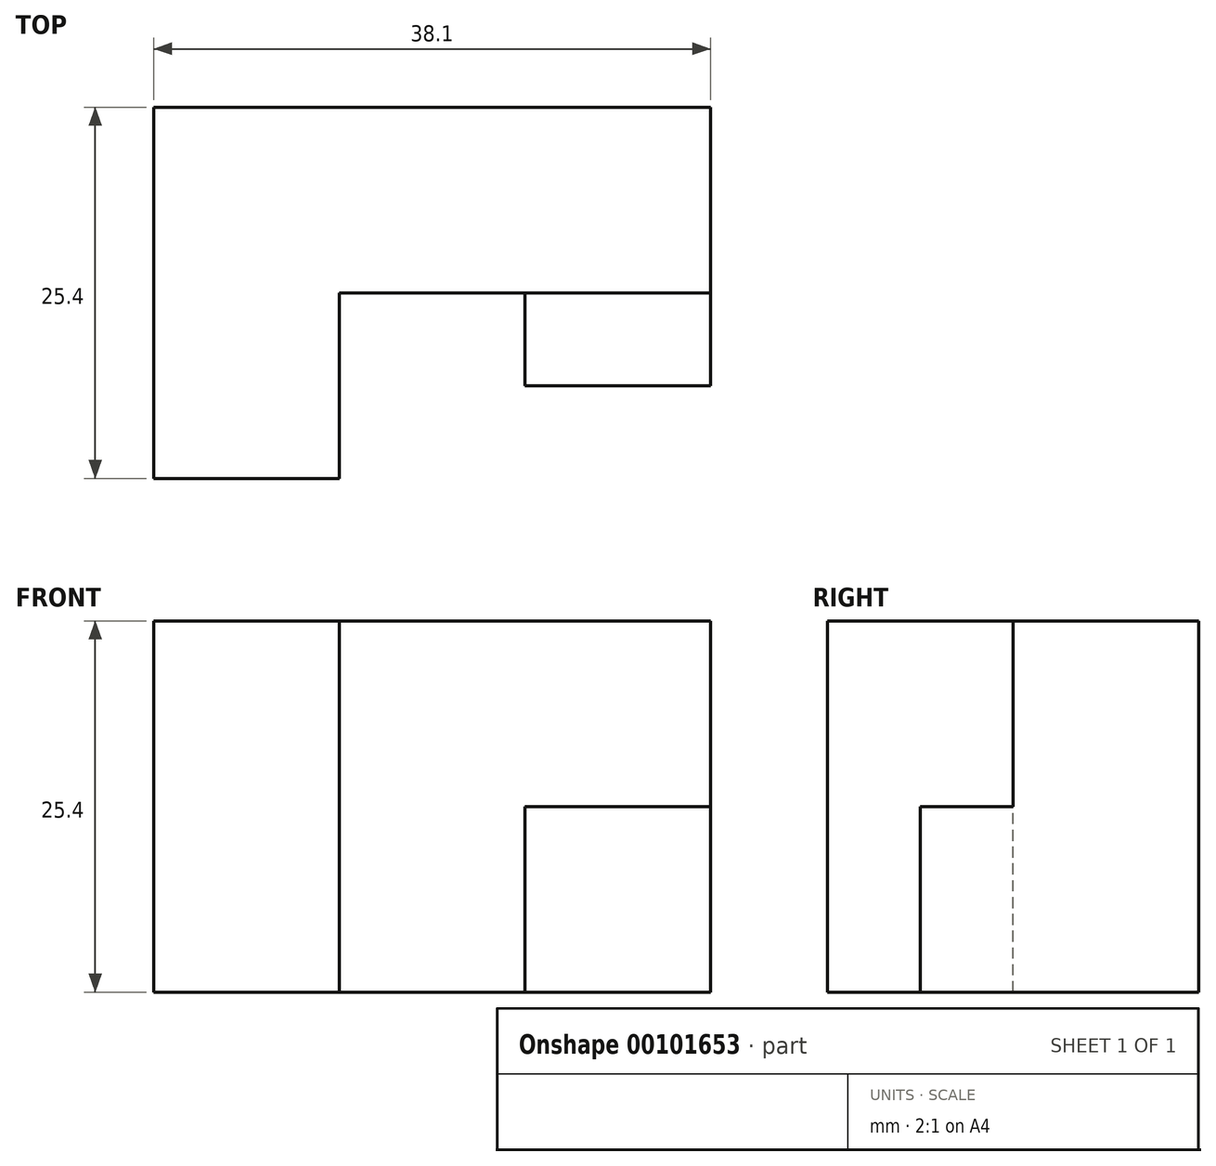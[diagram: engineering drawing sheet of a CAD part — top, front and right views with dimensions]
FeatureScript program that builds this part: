
annotation { "Feature Type Name" : "Feature", "Feature Type Description" : "" }
export const myFeature = defineFeature(function(context is Context, id is Id, definition is map)
    precondition{}
    {
        {
            var Q0;
            Q0=qCreatedBy(makeId("Front.planeOp"),FACE);
            var sketch = newSketch(context, id + "F0", { "sketchPlane" : qUnion([Q0])});
            skLineSegment(sketch, "E0", {"start": v(0, 0) * mm, "end": v(38.1, 0) * mm});
            skLineSegment(sketch, "E1", {"start": v(0, 25.4) * mm, "end": v(0, 0) * mm});
            skLineSegment(sketch, "E2", {"start": v(38.1, 0) * mm, "end": v(38.1, 12.7) * mm});
            skLineSegment(sketch, "E3", {"start": v(38.1, 12.7) * mm, "end": v(25.4, 12.7) * mm});
            skLineSegment(sketch, "E4", {"start": v(25.4, 12.7) * mm, "end": v(25.4, 0) * mm});
            skLineSegment(sketch, "E5", {"start": v(38.1, 12.7) * mm, "end": v(38.1, 25.4) * mm});
            skLineSegment(sketch, "E6", {"start": v(38.1, 25.4) * mm, "end": v(12.7, 25.4) * mm});
            skLineSegment(sketch, "E7", {"start": v(12.7, 25.4) * mm, "end": v(12.7, 0) * mm});
            skLineSegment(sketch, "E8", {"start": v(0, 25.4) * mm, "end": v(12.7, 25.4) * mm});
            skSolve(sketch);
        }
        {
            var Q0;
            Q0 = qSketchRegion(id + "F0", true);
            extrude(context, id + "F1", {"entities" : qUnion([Q0]), "depth" : 12.7 * mm});
        }
        {
            var Q0;
            {var subQ0=sQuery(id+"F0.wireOp",EDGE,"E1");Q0=makeQuery(id+"F0.imprint","IMPRINT",FACE,{"disambiguationData":[TD([[makeQuery(id+"F0.imprint","IMPRINT",EDGE,{"derivedFrom":subQ0}),1.0]])]});}
            extrude(context, id + "F2", {"entities" : qUnion([Q0]), "operationType" : NewBodyOperationType.ADD, "depth" : 25.4 * mm});
        }
        {
            var Q0;
            {var subQ0=sQuery(id+"F0.wireOp",EDGE,"E2");Q0=makeQuery(id+"F0.imprint","IMPRINT",FACE,{"disambiguationData":[TD([[makeQuery(id+"F0.imprint","IMPRINT",EDGE,{"derivedFrom":subQ0}),1.0]])]});}
            extrude(context, id + "F3", {"entities" : qUnion([Q0]), "operationType" : NewBodyOperationType.ADD, "depth" : 19.05 * mm});
        }
    });
